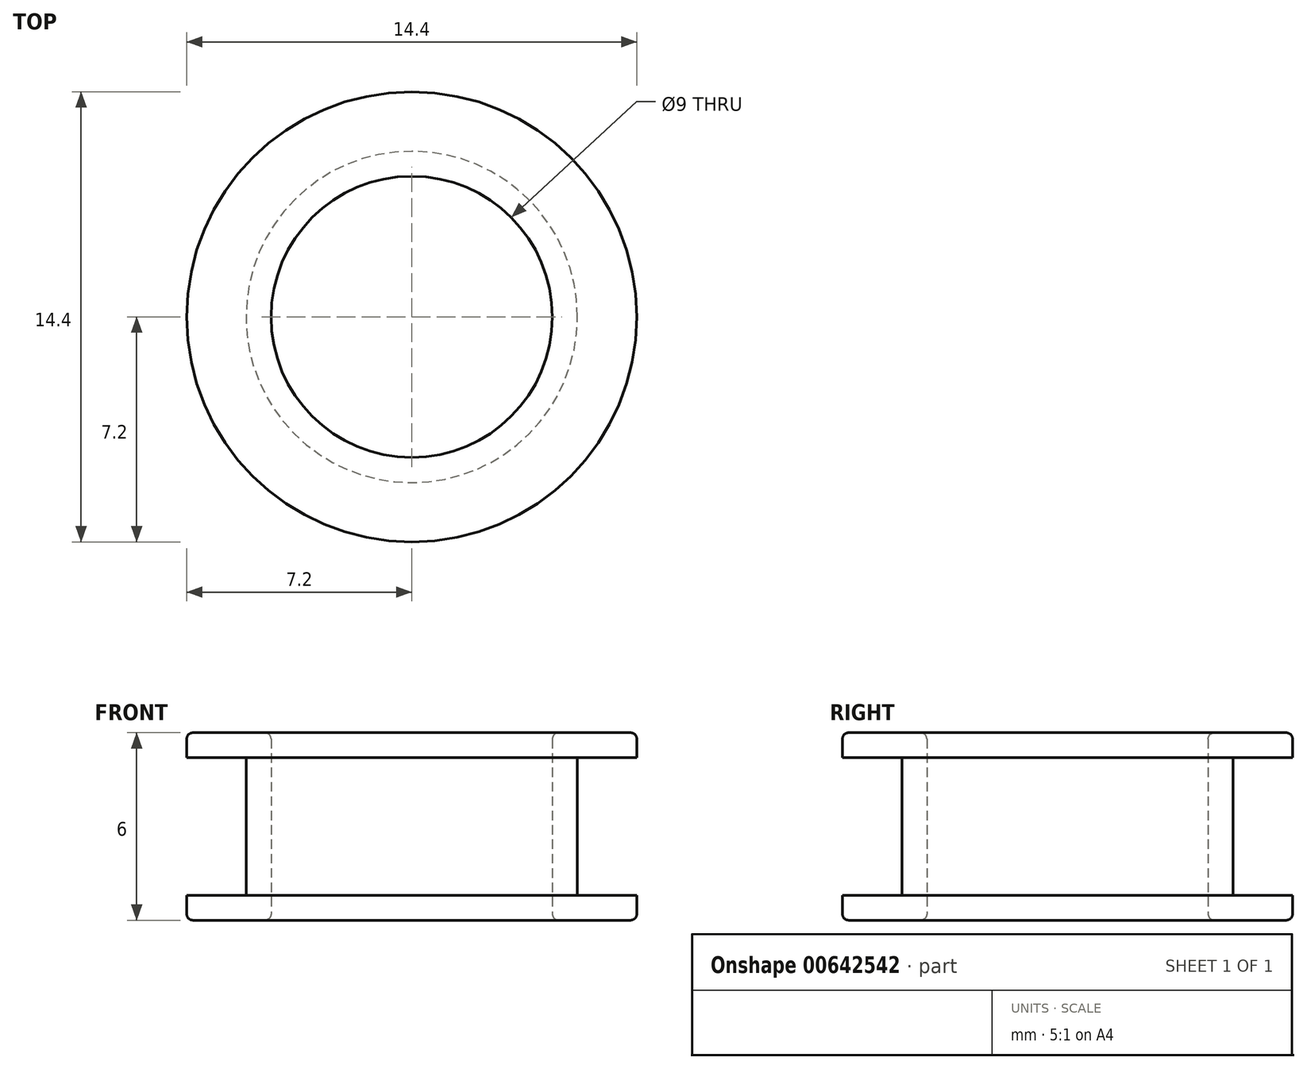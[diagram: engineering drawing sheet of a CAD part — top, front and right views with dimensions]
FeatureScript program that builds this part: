
annotation { "Feature Type Name" : "Feature", "Feature Type Description" : "" }
export const myFeature = defineFeature(function(context is Context, id is Id, definition is map)
    precondition{}
    {
        {
            var Q0;
            Q0=qCreatedBy(makeId("Top.planeOp"),FACE);
            var sketch = newSketch(context, id + "F0", { "sketchPlane" : qUnion([Q0])});
            skCircle(sketch, "E0", {"center": v(0, 0) * mm, "radius": 7.2 * mm});
            skSolve(sketch);
        }
        {
            var Q0;
            Q0 = qSketchRegion(id + "F0", true);
            extrude(context, id + "F1", {"entities" : qUnion([Q0]), "depth" : 6 * mm, "offsetDistance" : 25.4 * mm});
        }
        {
            var Q0;
            Q0=makeQuery(id+"F1.opExtrude","CAP_FACE",FACE,{"disambiguationData":[OSD([sQuery(id+"F0.wireOp",EDGE,"E0")])],"isStart":true});
            var sketch = newSketch(context, id + "F2", { "sketchPlane" : qUnion([Q0])});
            skCircle(sketch, "E1", {"center": v(0, 0) * mm, "radius": 4.5 * mm});
            skSolve(sketch);
        }
        {
            var Q0;
            Q0=makeQuery(id+"F2.imprint","IMPRINT",FACE,{"disambiguationData":[TD([[makeQuery(id+"F2.imprint","IMPRINT",EDGE,{"derivedFrom":sQuery(id+"F2.wireOp",EDGE,"E1")}),1.0]])]});
            extrude(context, id + "F3", {"entities" : qUnion([Q0]), "operationType" : NewBodyOperationType.REMOVE, "endBound" : BoundingType.THROUGH_ALL, "oppositeDirection" : true, "depth" : 25.4 * mm, "offsetDistance" : 25.4 * mm});
        }
        {
            var Q0;
            Q0=makeQuery(id+"F1.opExtrude","CAP_FACE",FACE,{"disambiguationData":[OSD([sQuery(id+"F0.wireOp",EDGE,"E0")])],"isStart":true});
            var Q1;
            Q1=makeQuery(id+"F1.opExtrude","CAP_FACE",FACE,{"disambiguationData":[OSD([sQuery(id+"F0.wireOp",EDGE,"E0")])],"isStart":false});
            fillet(context, id + "F4", {"entities" : qUnion([Q0, Q1]), "radius" : 0.2 * mm, "tangentPropagation" : true, "allowEdgeOverflow" : false});
        }
        {
            var Q0;
            Q0=makeQuery(id+"F1.opExtrude","SWEPT_FACE",FACE,{"disambiguationData":[OSD([sQuery(id+"F0.wireOp",EDGE,"E0")])]});
            shell(context, id + "F5", {"entities" : qUnion([Q0]), "thickness" : 0.8 * mm});
        }
    });
